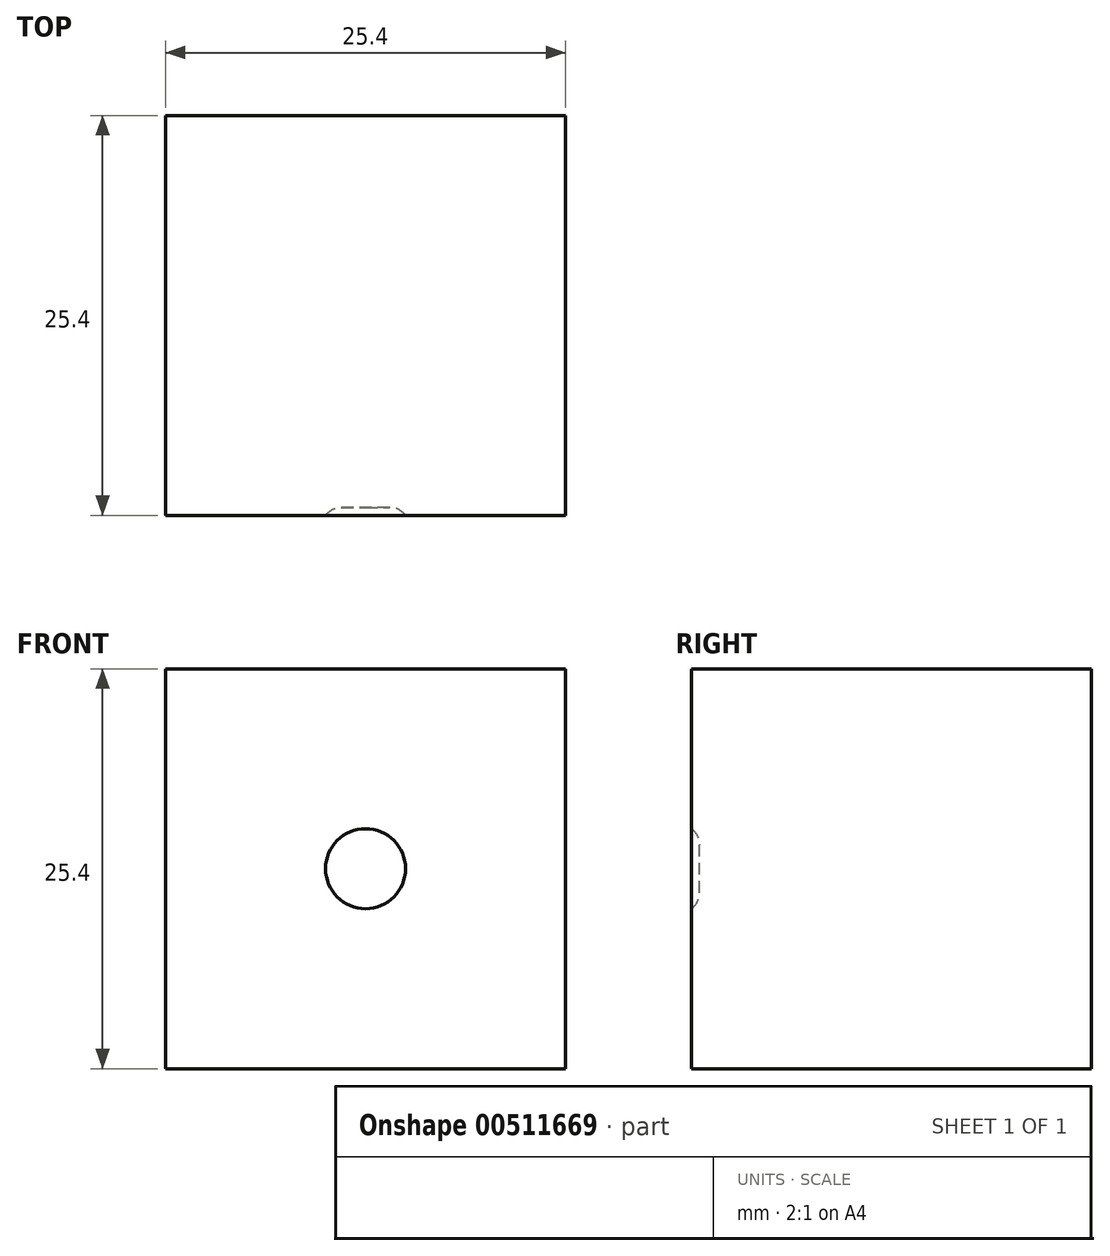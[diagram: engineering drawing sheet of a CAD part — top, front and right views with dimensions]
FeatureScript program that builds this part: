
annotation { "Feature Type Name" : "Feature", "Feature Type Description" : "" }
export const myFeature = defineFeature(function(context is Context, id is Id, definition is map)
    precondition{}
    {
        {
            var Q0;
            Q0=qCreatedBy(makeId("Front.planeOp"),FACE);
            var sketch = newSketch(context, id + "F0", { "sketchPlane" : qUnion([Q0])});
            skLineSegment(sketch, "E0.bottom", {"start": v(-12.7, -12.7) * mm, "end": v(12.7, -12.7) * mm});
            skLineSegment(sketch, "E0.top", {"start": v(-12.7, 12.7) * mm, "end": v(12.7, 12.7) * mm});
            skLineSegment(sketch, "E0.left", {"start": v(-12.7, -12.7) * mm, "end": v(-12.7, 12.7) * mm});
            skLineSegment(sketch, "E0.right", {"start": v(12.7, -12.7) * mm, "end": v(12.7, 12.7) * mm});
            skPoint(sketch, "E0.middle", {"position": v(0, 0) * mm});
            skSolve(sketch);
        }
        {
            var Q0;
            Q0=makeQuery(id+"F0.imprint","IMPRINT",FACE,{"disambiguationData":[TD([[makeQuery(id+"F0.imprint","IMPRINT",EDGE,{"derivedFrom":sQuery(id+"F0.wireOp",EDGE,"E0.bottom")}),1.0]])]});
            extrude(context, id + "F1", {"entities" : qUnion([Q0]), "depth" : 25.4 * mm});
        }
        {
            var Q0;
            Q0=makeQuery(id+"F1.opExtrude","CAP_FACE",FACE,{"disambiguationData":[OSD([sQuery(id+"F0.wireOp",EDGE,"E0.bottom"),sQuery(id+"F0.wireOp",EDGE,"E0.top"),sQuery(id+"F0.wireOp",EDGE,"E0.left"),sQuery(id+"F0.wireOp",EDGE,"E0.right")])],"isStart":false});
            var sketch = newSketch(context, id + "F2", { "sketchPlane" : qUnion([Q0])});
            skCircle(sketch, "E1", {"center": v(0, 0) * mm, "radius": 2.54 * mm});
            skSolve(sketch);
        }
        {
            var Q0;
            Q0=makeQuery(id+"F2.imprint","IMPRINT",FACE,{"disambiguationData":[TD([[makeQuery(id+"F2.imprint","IMPRINT",EDGE,{"derivedFrom":sQuery(id+"F2.wireOp",EDGE,"E1")}),1.0]])]});
            extrude(context, id + "F3", {"entities" : qUnion([Q0]), "operationType" : NewBodyOperationType.REMOVE, "oppositeDirection" : true, "depth" : 0.5 * mm});
        }
        {
            var Q0;
            Q0=makeQuery(id+"F3.boolean.opBoolean","COPY",FACE,{"derivedFrom":makeQuery(id+"F3.opExtrude","CAP_FACE",FACE,{"disambiguationData":[OSD([sQuery(id+"F2.wireOp",EDGE,"E1")])],"isStart":false})});
            fillet(context, id + "F4", {"entities" : qUnion([Q0]), "radius" : 1.27 * mm, "tangentPropagation" : true, "allowEdgeOverflow" : false});
        }
    });
